# Revit family: C_PPSDT160_3D_CAD_MULT_Prod
name_source: partatom
category: Structural Connections
revit_build: Autodesk Revit 2015 (Build: 20140606_1530(x64)
units: mm (PartAtom-declared; Revit-internal decimal feet)

## types (1)
- C_PPSDT160_3D_CAD_MULT_Prod
    Default Elevation = 0 mm  [stored 0 ft]
    Density = 0.77 kg
    Description = Post bases
    EPD = https://www.strongtie.eu
    ETA / DoP = https://www.strongtie.eu
    Manufacturer = Simpson Strong-Tie
    Model = PPSDT160
    Model Disclaimer = Contact Simpson Strong-Tie Company  for more information
    Model ID = 0081687875147547144262547762410679911027
    Name = PPSDT160
    ObjectType = PPSDT160
    Product Material = HotDipGalvanised
    Product Type = Post bases
    Reference = PPSDT160
    STD type1 = STD12X80
    STD type2 = STD12X100
    STD type3 = STD12X120
    STD type4 = STD12X140
    STD type5 = STD12X160
    STD type6 = STD12X180
    STD type7 = STD12X200
    Technical datasheet = https://www.strongtie.eu
    URL = www.strongtie.eu
    UniClass Number = Pr_20_29_31_45
    UniClass Title = Joist hangers

note: [stored X ft] marks values corroborated as IEEE doubles in the binary element streams (Revit-internal decimal feet)

## geometry (parser evidence)
native form markers: Blend x29, Sweep x13
no freeform markers — native parametric forms only
